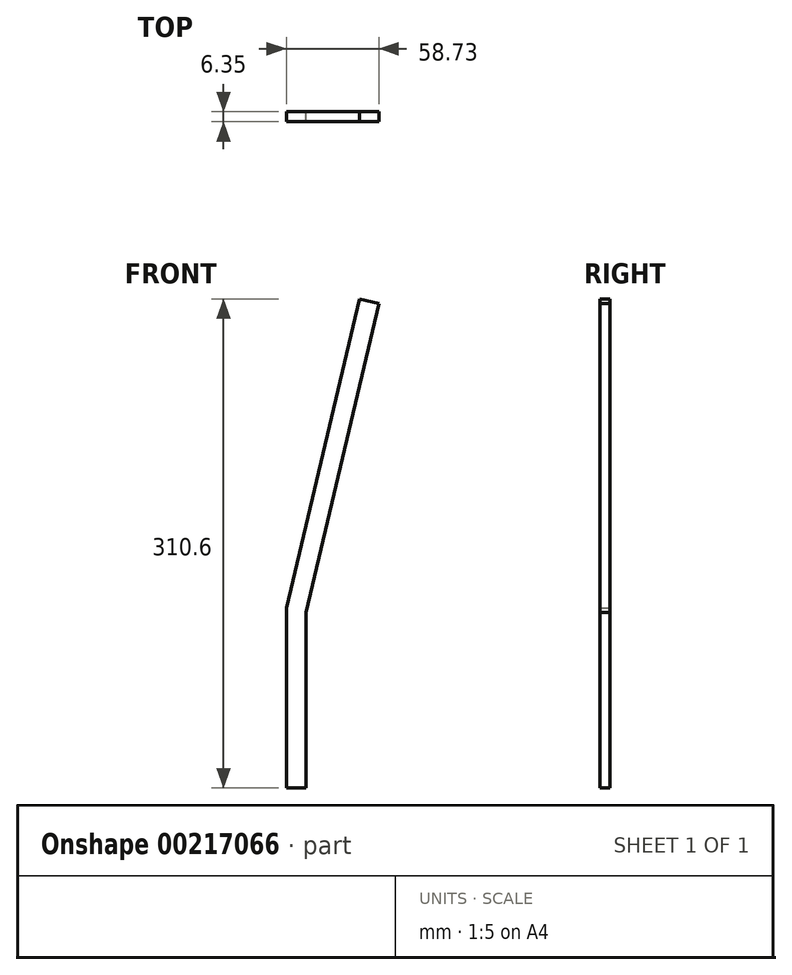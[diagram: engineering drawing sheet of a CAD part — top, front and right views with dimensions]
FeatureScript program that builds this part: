
annotation { "Feature Type Name" : "Feature", "Feature Type Description" : "" }
export const myFeature = defineFeature(function(context is Context, id is Id, definition is map)
    precondition{}
    {
        {
            var Q0;
            Q0=qCreatedBy(makeId("Front.planeOp"),FACE);
            var sketch = newSketch(context, id + "F0", { "sketchPlane" : qUnion([Q0])});
            skLineSegment(sketch, "E0", {"start": v(0, 0) * mm, "end": v(46.72, 197.76) * mm, "construction": true});
            skLineSegment(sketch, "E1", {"start": v(46.72, 197.76) * mm, "end": v(40.54, 199.22) * mm});
            skLineSegment(sketch, "E2", {"start": v(0, 0) * mm, "end": v(-12.36, 2.92) * mm});
            skLineSegment(sketch, "E3", {"start": v(0, 0) * mm, "end": v(12.36, -2.92) * mm});
            skLineSegment(sketch, "E4", {"start": v(46.72, 197.76) * mm, "end": v(52.9, 196.3) * mm});
            skLineSegment(sketch, "E5", {"start": v(-12.36, -111.38) * mm, "end": v(12.36, -111.38) * mm});
            skPoint(sketch, "E6.trimOffspring.end.orphan", {"position": v(12.36, -35.18) * mm});
            skPoint(sketch, "E7.end.orphan", {"position": v(-12.36, -35.18) * mm});
            skLineSegment(sketch, "E8", {"start": v(40.54, 199.22) * mm, "end": v(-5.83, 2.92) * mm});
            skLineSegment(sketch, "E9", {"start": v(52.9, 196.3) * mm, "end": v(6.52, 0) * mm});
            skLineSegment(sketch, "E10", {"start": v(6.52, 0) * mm, "end": v(6.52, -111.38) * mm});
            skLineSegment(sketch, "E11", {"start": v(-5.83, 2.92) * mm, "end": v(-5.83, -111.38) * mm});
            skPoint(sketch, "E12.center.orphan", {"position": v(0, -35.18) * mm});
            skSolve(sketch);
        }
        {
            var Q0;
            Q0 = qSketchRegion(id + "F0", true);
            extrude(context, id + "F1", {"entities" : qUnion([Q0]), "depth" : 6.35 * mm});
        }
    });
